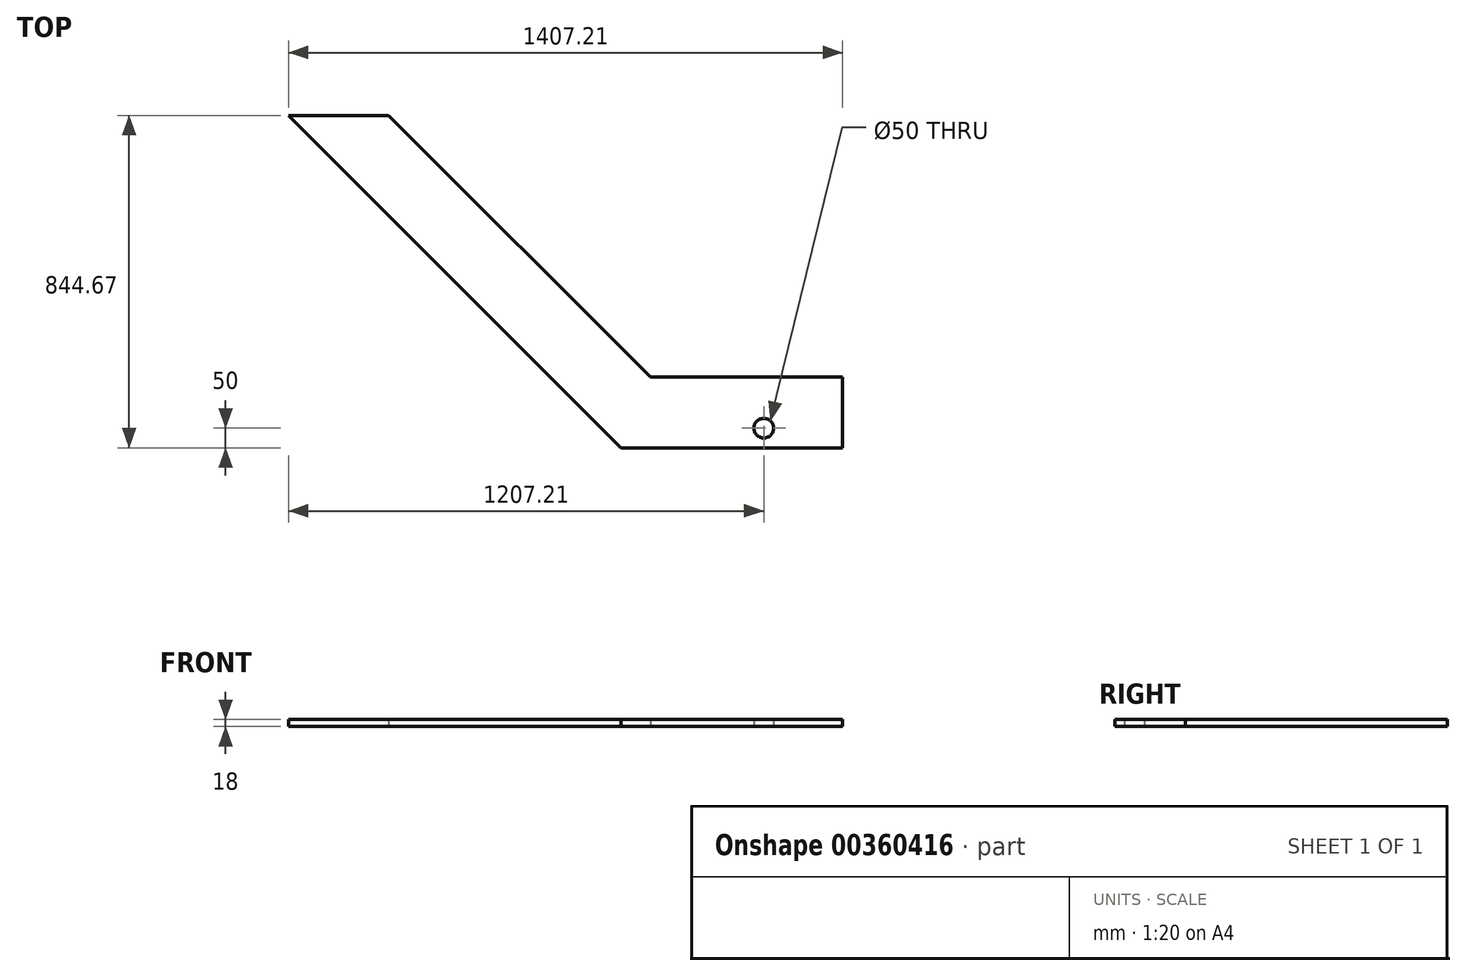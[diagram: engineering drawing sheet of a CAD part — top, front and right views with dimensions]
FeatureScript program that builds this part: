
annotation { "Feature Type Name" : "Feature", "Feature Type Description" : "" }
export const myFeature = defineFeature(function(context is Context, id is Id, definition is map)
    precondition{}
    {
        {
            var Q0;
            Q0=qCreatedBy(makeId("Top.planeOp"),FACE);
            var sketch = newSketch(context, id + "F0", { "sketchPlane" : qUnion([Q0])});
            skLineSegment(sketch, "E0", {"start": v(0, 0) * mm, "end": v(-562.54, 0) * mm});
            skLineSegment(sketch, "E1", {"start": v(-562.54, 0) * mm, "end": v(-1407.21, 844.67) * mm});
            skLineSegment(sketch, "E2", {"start": v(-1407.21, 844.67) * mm, "end": v(-1152.66, 844.67) * mm});
            skLineSegment(sketch, "E3", {"start": v(-1152.66, 844.67) * mm, "end": v(-487.99, 180) * mm});
            skLineSegment(sketch, "E4", {"start": v(-487.99, 180) * mm, "end": v(0, 180) * mm});
            skLineSegment(sketch, "E5", {"start": v(0, 180) * mm, "end": v(0, 0) * mm});
            skLineSegment(sketch, "E6", {"start": v(0, 1382) * mm, "end": v(0, 180) * mm, "construction": true});
            skCircle(sketch, "E7", {"center": v(-200, 50) * mm, "radius": 25 * mm});
            skLineSegment(sketch, "E8", {"start": v(0, -18) * mm, "end": v(-570, -18) * mm, "construction": true});
            skLineSegment(sketch, "E9", {"start": v(-570, -18) * mm, "end": v(-1432.67, 844.67) * mm, "construction": true});
            skLineSegment(sketch, "E10", {"start": v(-1170.66, 862.67) * mm, "end": v(-1432.67, 862.67) * mm, "construction": true});
            skLineSegment(sketch, "E11", {"start": v(-1432.67, 862.67) * mm, "end": v(-1432.67, 844.67) * mm});
            skSolve(sketch);
        }
        {
            var Q0;
            Q0=makeQuery(id+"F0.imprint","IMPRINT",FACE,{"disambiguationData":[TD([[makeQuery(id+"F0.imprint","IMPRINT",EDGE,{"derivedFrom":sQuery(id+"F0.wireOp",EDGE,"E0")}),-1.0]])]});
            extrude(context, id + "F1", {"entities" : qUnion([Q0]), "depth" : 18 * mm});
        }
    });
